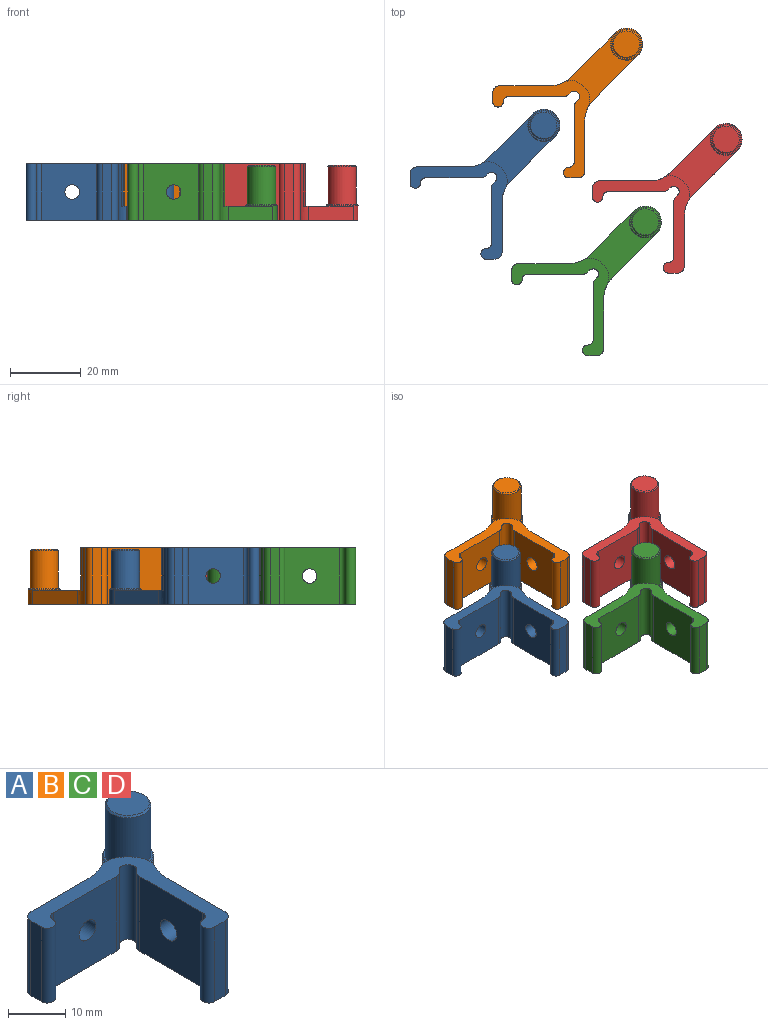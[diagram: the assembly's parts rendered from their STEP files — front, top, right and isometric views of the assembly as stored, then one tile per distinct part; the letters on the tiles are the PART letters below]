
ASSEMBLY  parts=4 mates=3
PART A: 35 faces, bbox 42.2x42.2x16 mm
  f0: cylinder r=1.5mm len=16mm, axis (0,0,-1), area 37.7mm2, adj f1,f21,f23,f32
  f1: plane 16x15.55mm, normal (0,-1,0), area 235.6mm2, adj f0,f2,f23,f32,f33
  f2: cylinder r=2mm len=16mm, axis (0,0,-1), area 25.1mm2, adj f1,f3,f23,f32
  f3: plane 16x0.48mm, normal (0.71,-0.71,0), area 10.7mm2, adj f2,f4,f23,f32
  f4: cylinder r=1.5mm len=16mm, axis (0,0,-1), area 75.4mm2, adj f3,f5,f23,f32
  f5: plane 16x0.48mm, normal (-0.71,0.71,0), area 10.7mm2, adj f4,f6,f23,f32
  f6: cylinder r=2mm len=16mm, axis (0,0,-1), area 25.1mm2, adj f5,f7,f23,f32
  f7: plane 16x15.55mm, normal (-1,0,0), area 235.6mm2, adj f6,f8,f23,f32,f34
  f8: cylinder r=1.5mm len=16mm, axis (0,0,-1), area 37.7mm2, adj f7,f9,f23,f32
  f9: cylinder r=1.5mm len=16mm, axis (0,0,-1), area 75.4mm2, adj f8,f10,f23,f32
  f10: plane 16x2.5mm, normal (0,-1,0), area 40mm2, adj f9,f11,f23,f32
  f11: cylinder r=2mm len=16mm, axis (0,0,-1), area 50.3mm2, adj f10,f12,f23,f32
  f12: plane 16x14.32mm, normal (1,0,0), area 216mm2, adj f11,f13,f23,f32,f34
  f13: cylinder r=8mm len=16mm, axis (0,0,-1), area 71.7mm2, adj f12,f14,f22,f23,f29,f32
  f14: plane 12.59x12.59mm, normal (0.71,-0.71,0), area 71.2mm2, adj f13,f15,f22,f23
  f15: cylinder r=4.5mm len=9mm, axis (0,0,-1), area 65mm2, adj f14,f16,f22,f23,f25
  f16: plane 12.59x12.59mm, normal (-0.71,0.71,0), area 71.2mm2, adj f15,f17,f22,f23
  f17: cylinder r=8mm len=16mm, axis (0,0,-1), area 71.7mm2, adj f16,f18,f22,f23,f31,f32
  f18: plane 16x14.32mm, normal (0,1,0), area 216mm2, adj f17,f19,f23,f32,f33
  f19: cylinder r=2mm len=16mm, axis (0,0,-1), area 50.3mm2, adj f18,f20,f23,f32
  f20: plane 16x2.5mm, normal (-1,0,0), area 40mm2, adj f19,f21,f23,f32
  f21: cylinder r=1.5mm len=16mm, axis (0,0,-1), area 75.4mm2, adj f0,f20,f23,f32
  f22: plane 20.88x20.88mm, normal (0,0,1), area 126.7mm2, adj f13,f14,f15,f16,f17,f29,f30,f31
  f23: plane 42.25x42.25mm, normal (0,0,-1), area 360.7mm2, adj f0,f1,f2,f3,f4,f5,f6,f7
  f24: plane 8.6x8.6mm, normal (0,0,1), area 7.8mm2, adj f25,f26
  f25: cone r=4.3mm half-angle=45deg, axis (0,0,-1), area 7.8mm2, adj f15,f24
  f26: cylinder r=4mm len=10.7mm, axis (0,0,-1), area 268.9mm2, adj f24,f28
  f27: plane 7.4x7.4mm, normal (0,0,1), area 43mm2, adj f28
  f28: cone r=3.7mm half-angle=45deg, axis (0,0,-1), area 10.3mm2, adj f26,f27
  f29: cylinder r=4.5mm len=12mm, axis (0,0,-1), area 68.7mm2, adj f13,f22,f30,f32
  f30: plane 12x0.79mm, normal (0.71,0.71,0), area 13.4mm2, adj f22,f29,f31,f32
  f31: cylinder r=4.5mm len=12mm, axis (0,0,-1), area 68.7mm2, adj f17,f22,f30,f32
  f32: plane 27.44x27.44mm, normal (0,0,1), area 170.4mm2, adj f0,f1,f2,f3,f4,f5,f6,f7
  f33: cylinder r=2.05mm len=4.1mm, axis (0,1,0), area 38.6mm2, adj f1,f18
  f34: cylinder r=2.05mm len=4.1mm, axis (1,0,0), area 38.6mm2, adj f7,f12
PART B: same geometry as A
PART C: same geometry as A
PART D: same geometry as A
PLACE A t=(-17.8,-12.39,-24.06)mm
PLACE B t=(5.53,10.52,-24.06)mm
PLACE C t=(10.88,-39.64,-24.06)mm
PLACE D t=(33.62,-16.34,-24.06)mm
MATE planar B.f23 <-> C.f23  axis (0,0,-1) through (18.37,23.36,-24.06)mm
MATE planar C.f23 <-> D.f23  axis (0,0,-1) through (23.72,-26.79,-24.06)mm
MATE planar A.f23 <-> B.f23  axis (0,0,-1) through (-4.96,0.45,-24.06)mm
